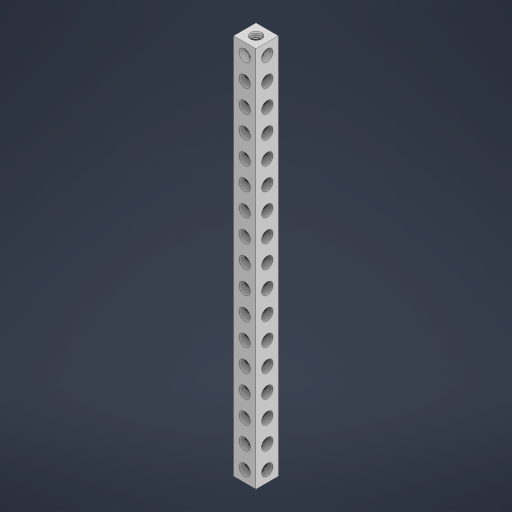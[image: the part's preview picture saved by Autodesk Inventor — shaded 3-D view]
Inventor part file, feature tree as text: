
AUTODESK INVENTOR PART (.ipt)
format: ipt  version: 2023 (Build 270158000, 158)  size: 1,265,152 bytes
history: native  units: in
note: dims shown in document units (in); Inventor stores cm internally (conversion verified against a paired STEP export)
features: mirror x1
ambient origin geometry x8: Origin, YZ Plane, XZ Plane, XY Plane, X Axis, Y Axis, Z Axis, Center Point
bodies: Solid1 (feature_tree)
feature tree (1):
  mirror  "Mirror3"
